# Revit family: 0048748 Feilo Sylvania Lighting Fixture SYLPRF SUP LED G3 1500MM S 4K QC
name_source: partatom
category: Lighting Fixtures
revit_build: Autodesk Revit 2017 (Build: 20190507_1515(x64)
units: mm (PartAtom-declared; Revit-internal decimal feet)

## family parameters
Cut with Voids When Loaded = Yes
Host = Face
Light Source = Yes
OmniClass Number = 23.80.70.11.14
OmniClass Title = General Luminaries, Directional
Part Type = Normal
Room Calculation Point = No
Round Connector Dimension = Use Diameter
Shared = No

## types (1)
- 0048748 Feilo Sylvania Lighting Fixture SYLPRF SUP LED G3 1500MM S 4K QC
    AccessoryMaterial = Diffuser-Sylvania-Glow
    Apparent Load = 31 VA
    Assembly Code = D5020200
    AssetType = Fixed
    BodyMaterial = Body-Sylvania-Gray
    ClassificationName = Uniclass2015
    ClassificationValue = EF_70_80
    Color Filter = 16777215
    Cost = 0 $
    Default Elevation = 1219 mm
    DiffuserMaterial = Diffuser-Sylvania-Transparent
    Dimming Lamp Color Temperature Shift = <None>
    DimmingControlOptions = Non dimmable
    DocumentationLiterature = http://www.sylvania-lighting.com
    DurationUnit = hours
    ElectricShockClassification = Class I
    Emit Shape Visible in Rendering = No
    Emit from Rectangle Length = 1552 mm  [stored 5.09186 ft]
    Emit from Rectangle Width = 64 mm  [stored 0.209974 ft]
    ExpectedLife = 50000
    IfcExportAs = IfcLightFixtureType
    IfcExportType = IfcLightFixtureType
    ImpactProtectionIndex = IK08
    IngressProtection = IP65
    InputNominalFrequency = 50/60 Hz
    InputVoltage = 220-240V~
    Keynote = 16500
    Lamp = LED
    LampColourRenderingIndex = 80
    LampColourTemperature = 4000 K
    LampMacAdamStep = 3
    LampNominalLuminous = 4800 lm
    LampsType = LED
    Length = 1572 mm
    LuminaireType = Weatherproof
    LuminousEfficacy = 155 lm/W
    Manufacturer = Feilo Sylvania
    ManufacturerName = Feilo Sylvania
    Material = polycarbonate housing, polycarbonate diffuser
    Model = SYLPRF SUP LED G3 1500MM S 4K QC
    ModelNumber = 0048748
    ModelReference = SYLPRF SUP LED G3 1500MM S 4K QC
    Name = SYLPRF SUP LED G3 1500MM S 4K QC
    NominalHeight = 75 mm
    NominalLength = 1578 mm
    NominalWidth = 0 mm  [stored 0 ft]
    Photometric Web File = 0048748-C.ies
    PowerConsumption = 31 W
    PowerFactor = 0
    ReflectorMaterial = <By Category>
    Tilt Angle = -90.00°
    Type Image = <None>
    TypeName = SYLPRF SUP LED G3 1500MM S 4K QC
    URL = http://www.sylvania-lighting.com
    Voltage = 230 V
    Weight = 2.09 kg
    Width = 84 mm

note: [stored X ft] marks values corroborated as IEEE doubles in the binary element streams (Revit-internal decimal feet)

## geometry (parser evidence)
native form markers: Blend x4, Sweep x5
no freeform markers — native parametric forms only
